# Revit family: 797210001_Filtro en Y 1-2P
name_source: partatom
category: Pipe Accessories
units: mm (PartAtom-declared; Revit-internal decimal feet)

## family parameters
Always vertical = Yes
Cut with Voids When Loaded = No
OmniClass Number = 23.27.55.29.17
OmniClass Title = Y Strainers
Part Type = Valve - Normal
Round Connector Dimension = Use Diameter
Shared = No
Work Plane-Based = No

## types (1)
- Filtro En Y 1/2P
    Alto = 46.4 mm  [stored 0.152231 ft]
    Ancho = 25.7 mm  [stored 0.0843176 ft]
    Creado por = BIMBAU
    Cuidado Y Limpieza = Limpiar con un paño húmedo. - No se debe limpiar con elementos abrasivos como esponjas 
 de alambre,ácidos o disolventes.
    Default Elevation = 0 mm  [stored 0 ft]
    Description = Producto para todo tipo de instalación- Producto que no contamina el agua.
    Fecha de creación = 11/03/2021
    Longitud = 59.2 mm  [stored 0.194226 ft]
    Manufacturer = Grival
    Material = Corona_Laton_Cobre
    Model = Filtro en Y 1/2P
    Peso Bruto aprox = 160gr. / 0,35Lb.
    Peso Neto aprox = 140gr. / 0,31Lb.
    Presion maxima = 125 Psi.
    Presion minima = 5 Psi.
    Referencia = 797210001
    Temperaturas máxima de trabajo = 51,7 ºC / 125,06 ºF.
    Temperaturas mínima de trabajo = 4 ºC / 39,2 ºF.
    URL = https://www.grival.com

note: [stored X ft] marks values corroborated as IEEE doubles in the binary element streams (Revit-internal decimal feet)

## geometry (parser evidence)
native form markers: Sweep x2
no freeform markers — native parametric forms only
